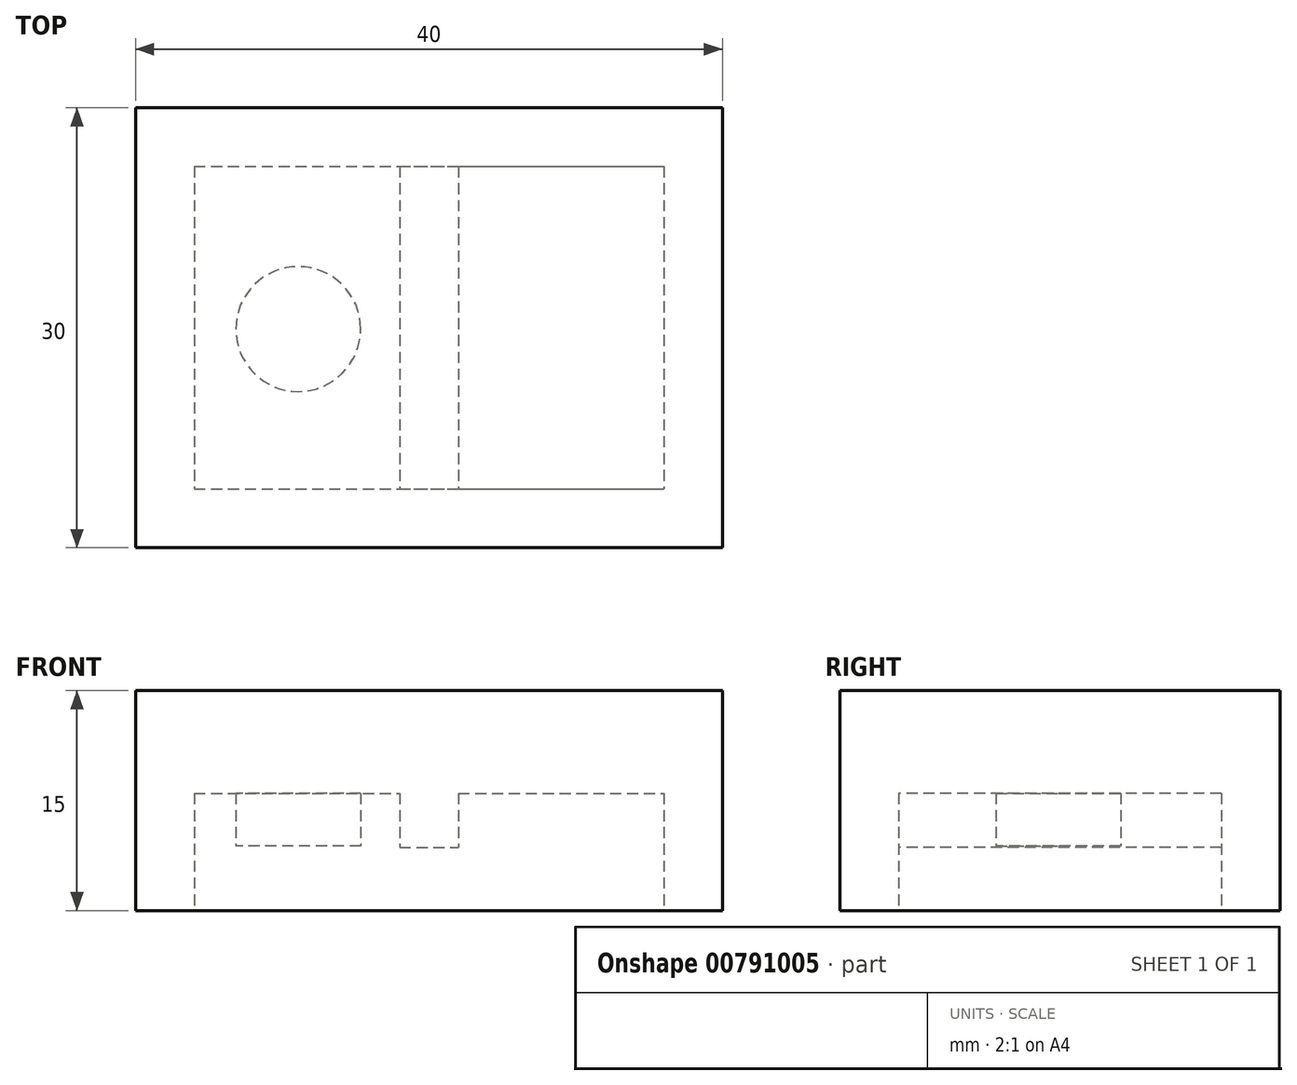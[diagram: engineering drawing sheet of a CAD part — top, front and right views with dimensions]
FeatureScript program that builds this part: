
annotation { "Feature Type Name" : "Feature", "Feature Type Description" : "" }
export const myFeature = defineFeature(function(context is Context, id is Id, definition is map)
    precondition{}
    {
        {
            var Q0;
            Q0=qCreatedBy(makeId("Top.planeOp"),FACE);
            var sketch = newSketch(context, id + "F0", { "sketchPlane" : qUnion([Q0])});
            skLineSegment(sketch, "E0.bottom", {"start": v(-22.46, 7.3) * mm, "end": v(17.54, 7.3) * mm});
            skLineSegment(sketch, "E0.top", {"start": v(-22.46, -22.7) * mm, "end": v(17.54, -22.7) * mm});
            skLineSegment(sketch, "E0.left", {"start": v(-22.46, 7.3) * mm, "end": v(-22.46, -22.7) * mm});
            skLineSegment(sketch, "E0.right", {"start": v(17.54, 7.3) * mm, "end": v(17.54, -22.7) * mm});
            skLineSegment(sketch, "E1.bottom", {"start": v(-18.46, 3.3) * mm, "end": v(13.54, 3.3) * mm});
            skLineSegment(sketch, "E1.top", {"start": v(-18.46, -18.7) * mm, "end": v(13.54, -18.7) * mm});
            skLineSegment(sketch, "E1.left", {"start": v(-18.46, 3.3) * mm, "end": v(-18.46, -18.7) * mm});
            skLineSegment(sketch, "E1.right", {"start": v(13.54, 3.3) * mm, "end": v(13.54, -18.7) * mm});
            skLineSegment(sketch, "E2.bottom", {"start": v(-4.46, 3.3) * mm, "end": v(-0.46, 3.3) * mm});
            skLineSegment(sketch, "E2.top", {"start": v(-4.46, -18.7) * mm, "end": v(-0.46, -18.7) * mm});
            skLineSegment(sketch, "E2.left", {"start": v(-4.46, 3.3) * mm, "end": v(-4.46, -18.7) * mm});
            skLineSegment(sketch, "E2.right", {"start": v(-0.46, 3.3) * mm, "end": v(-0.46, -18.7) * mm});
            skPoint(sketch, "E3", {"position": v(-2.46, 3.3) * mm});
            skCircle(sketch, "E4", {"center": v(-11.37, -7.79) * mm, "radius": 4.26 * mm});
            skSolve(sketch);
        }
        {
            var Q0;
            {var subQ1=sQuery(id+"F0.wireOp",EDGE,"E1.left");Q0=makeQuery(id+"F0.imprint","IMPRINT",FACE,{"disambiguationData":[TD([[makeQuery(id+"F0.imprint","IMPRINT",EDGE,{"derivedFrom":subQ1}),1.0]])]});}
            var Q1;
            {var subQ2=sQuery(id+"F0.wireOp",EDGE,"E1.right");Q1=makeQuery(id+"F0.imprint","IMPRINT",FACE,{"disambiguationData":[TD([[makeQuery(id+"F0.imprint","IMPRINT",EDGE,{"derivedFrom":subQ2}),-1.0]])]});}
            var Q2;
            {var subQ2=sQuery(id+"F0.wireOp",EDGE,"E2.left");Q2=makeQuery(id+"F0.imprint","IMPRINT",FACE,{"disambiguationData":[TD([[makeQuery(id+"F0.imprint","IMPRINT",EDGE,{"derivedFrom":subQ2}),1.0]])]});}
            var Q3;
            Q3=makeQuery(id+"F0.imprint","IMPRINT",FACE,{"disambiguationData":[TD([[makeQuery(id+"F0.imprint","IMPRINT",EDGE,{"derivedFrom":sQuery(id+"F0.wireOp",EDGE,"E0.bottom")}),-1.0]])]});
            var Q4;
            Q4=makeQuery(id+"F0.imprint","IMPRINT",FACE,{"disambiguationData":[TD([[makeQuery(id+"F0.imprint","IMPRINT",EDGE,{"derivedFrom":sQuery(id+"F0.wireOp",EDGE,"E4")}),1.0]])]});
            extrude(context, id + "F1", {"entities" : qUnion([Q0, Q1, Q2, Q3, Q4]), "depth" : 15 * mm, "offsetDistance" : 25 * mm});
        }
        {
            var Q0;
            {var subQ2=sQuery(id+"F0.wireOp",EDGE,"E1.right");Q0=makeQuery(id+"F0.imprint","IMPRINT",FACE,{"disambiguationData":[TD([[makeQuery(id+"F0.imprint","IMPRINT",EDGE,{"derivedFrom":subQ2}),-1.0]])]});}
            var Q1;
            {var subQ1=sQuery(id+"F0.wireOp",EDGE,"E1.left");Q1=makeQuery(id+"F0.imprint","IMPRINT",FACE,{"disambiguationData":[TD([[makeQuery(id+"F0.imprint","IMPRINT",EDGE,{"derivedFrom":subQ1}),1.0]])]});}
            extrude(context, id + "F2", {"entities" : qUnion([Q0, Q1]), "operationType" : NewBodyOperationType.REMOVE, "depth" : 8 * mm, "offsetDistance" : 25 * mm});
        }
        {
            var Q0;
            Q0=makeQuery(id+"F0.imprint","IMPRINT",FACE,{"disambiguationData":[TD([[makeQuery(id+"F0.imprint","IMPRINT",EDGE,{"derivedFrom":sQuery(id+"F0.wireOp",EDGE,"E4")}),1.0]])]});
            extrude(context, id + "F3", {"entities" : qUnion([Q0]), "operationType" : NewBodyOperationType.REMOVE, "depth" : 4.4 * mm, "offsetDistance" : 25 * mm});
        }
        {
            var Q0;
            {var subQ2=sQuery(id+"F0.wireOp",EDGE,"E2.left");Q0=makeQuery(id+"F0.imprint","IMPRINT",FACE,{"disambiguationData":[TD([[makeQuery(id+"F0.imprint","IMPRINT",EDGE,{"derivedFrom":subQ2}),1.0]])]});}
            extrude(context, id + "F4", {"entities" : qUnion([Q0]), "operationType" : NewBodyOperationType.REMOVE, "depth" : 4.3 * mm, "offsetDistance" : 25 * mm});
        }
    });
